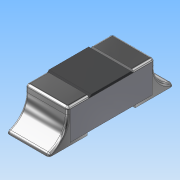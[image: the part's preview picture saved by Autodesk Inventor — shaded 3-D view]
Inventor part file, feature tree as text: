
AUTODESK INVENTOR PART (.ipt)
format: ipt  version: 2016 (Build 200138000, 138)  size: 207,872 bytes
history: native  units: mm
features: extrude x2, fillet x2, sketch x1, mirror x1
ambient origin geometry x8: Origin, YZ Plane, XZ Plane, XY Plane, X Axis, Y Axis, Z Axis, Center Point
bodies: Body1 (feature_tree)
feature tree (6):
  sketch  "Sketch10"  dims[d9=0.499mm d10=0.0mm d11=0.2mm d12=0.45mm d13=0.03mm d14=0.03mm d15=0.25mm d16=45.0deg d17=0.5mm d18=0.0mm d19=0.03mm d21=1.0mm d22=0.4mm d23=0.3mm d24=0.029mm]
  extrude  "Extrusion4"  Depth=0.2mm
  extrude  "Extrusion5"  Depth=0.45mm
  fillet  "Fillet2"  Radius=0.03mm
  fillet  "Fillet3"  Radius=0.03mm
  mirror  "Mirror1"
